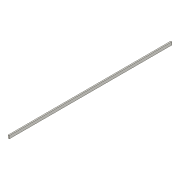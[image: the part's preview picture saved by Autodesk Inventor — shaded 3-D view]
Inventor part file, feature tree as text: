
AUTODESK INVENTOR PART (.ipt)
format: ipt  version: 2018 (Build 220112000, 112)  size: 71,168 bytes
history: native  units: in
note: dims shown in document units (in); Inventor stores cm internally (conversion verified against a paired STEP export)
features: extrude x1, sketch x1
ambient origin geometry x8: Origin, YZ Plane, XZ Plane, XY Plane, X Axis, Y Axis, Z Axis, Center Point
bodies: Solid1 (feature_tree)
feature tree (2):
  extrude  "Extrusion1"  Depth=2.0in
  sketch  "Sketch1"  dims[d0=5.0in d1=2.0in d2=284.0in d3=0.0in]
